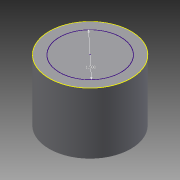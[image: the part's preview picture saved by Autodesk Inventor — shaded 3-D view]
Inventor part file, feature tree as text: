
AUTODESK INVENTOR PART (.ipt)
format: ipt  version: 2014 (Build 180170000, 170)  size: 72,192 bytes
history: native  units: in
note: dims shown in document units (in); Inventor stores cm internally (conversion verified against a paired STEP export)
features: sketch x2, extrude x1
ambient origin geometry x8: Origin, YZ Plane, XZ Plane, XY Plane, X Axis, Y Axis, Z Axis, Center Point
bodies: Solid1 (feature_tree)
feature tree (3):
  extrude  "Extrusion1"  Depth=1.5in TaperAngle=0.0deg
  sketch  "Sketch3"  dims[d6=1.5in]
  sketch  "Sketch1"  dims[d0=2.0in d1=1.5in d2=0.0in]
